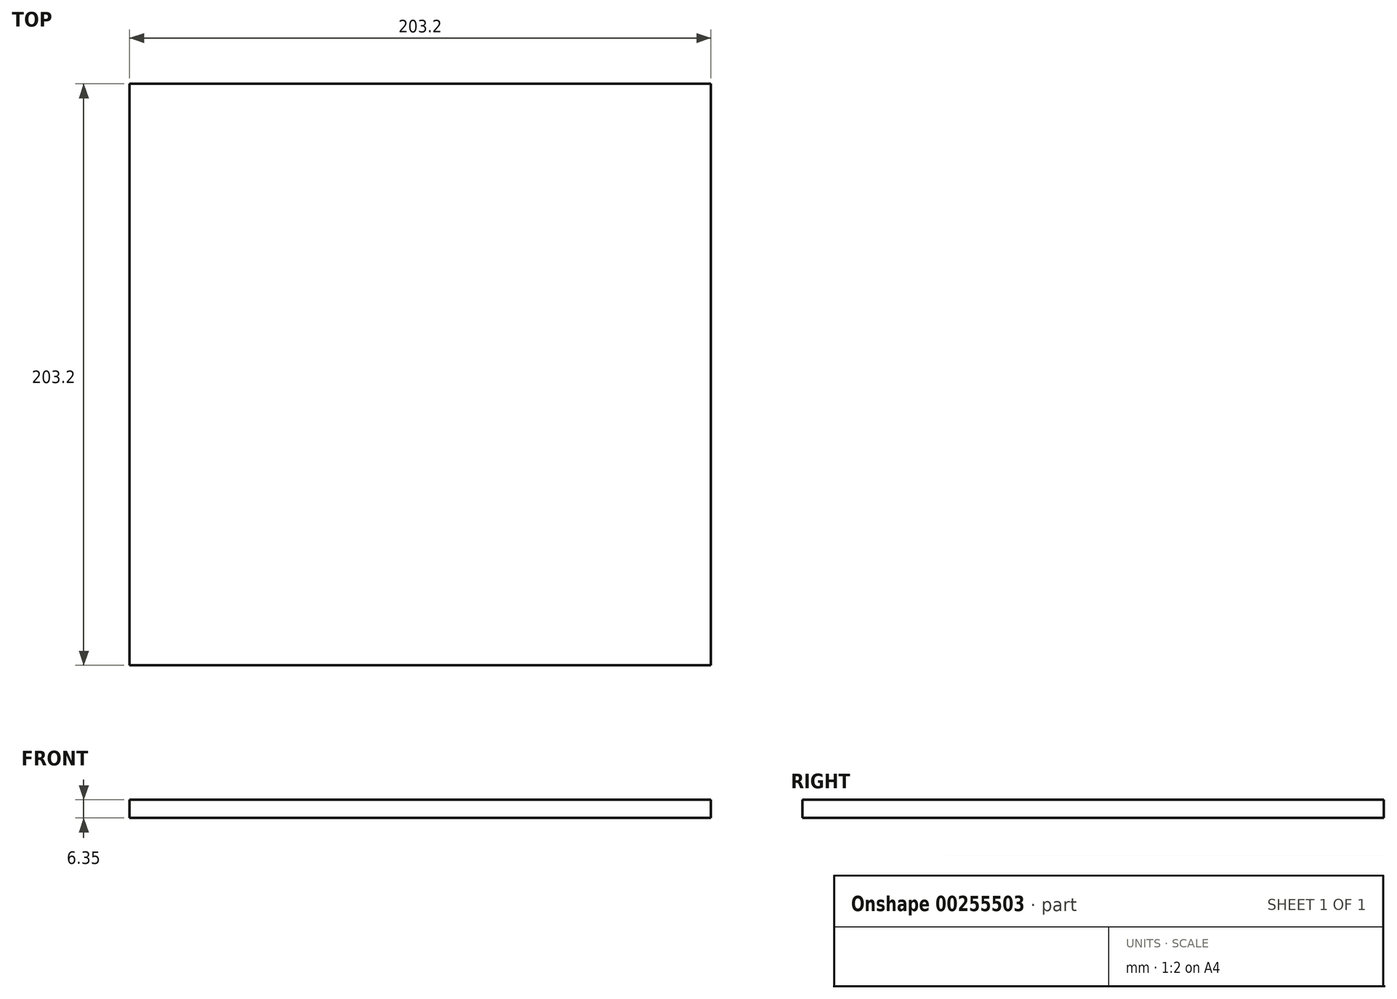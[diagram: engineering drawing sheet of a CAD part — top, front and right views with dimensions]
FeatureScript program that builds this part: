
annotation { "Feature Type Name" : "Feature", "Feature Type Description" : "" }
export const myFeature = defineFeature(function(context is Context, id is Id, definition is map)
    precondition{}
    {
        {
            var Q0;
            Q0=qCreatedBy(makeId("Top.planeOp"),FACE);
            var sketch = newSketch(context, id + "F0", { "sketchPlane" : qUnion([Q0])});
            skLineSegment(sketch, "E0.bottom", {"start": v(-101.6, 101.6) * mm, "end": v(101.6, 101.6) * mm});
            skLineSegment(sketch, "E0.top", {"start": v(-101.6, -101.6) * mm, "end": v(101.6, -101.6) * mm});
            skLineSegment(sketch, "E0.left", {"start": v(-101.6, 101.6) * mm, "end": v(-101.6, -101.6) * mm});
            skLineSegment(sketch, "E0.right", {"start": v(101.6, 101.6) * mm, "end": v(101.6, -101.6) * mm});
            skSolve(sketch);
        }
        {
            var Q0;
            Q0 = qSketchRegion(id + "F0", true);
            extrude(context, id + "F1", {"entities" : qUnion([Q0]), "depth" : 6.35 * mm});
        }
    });
